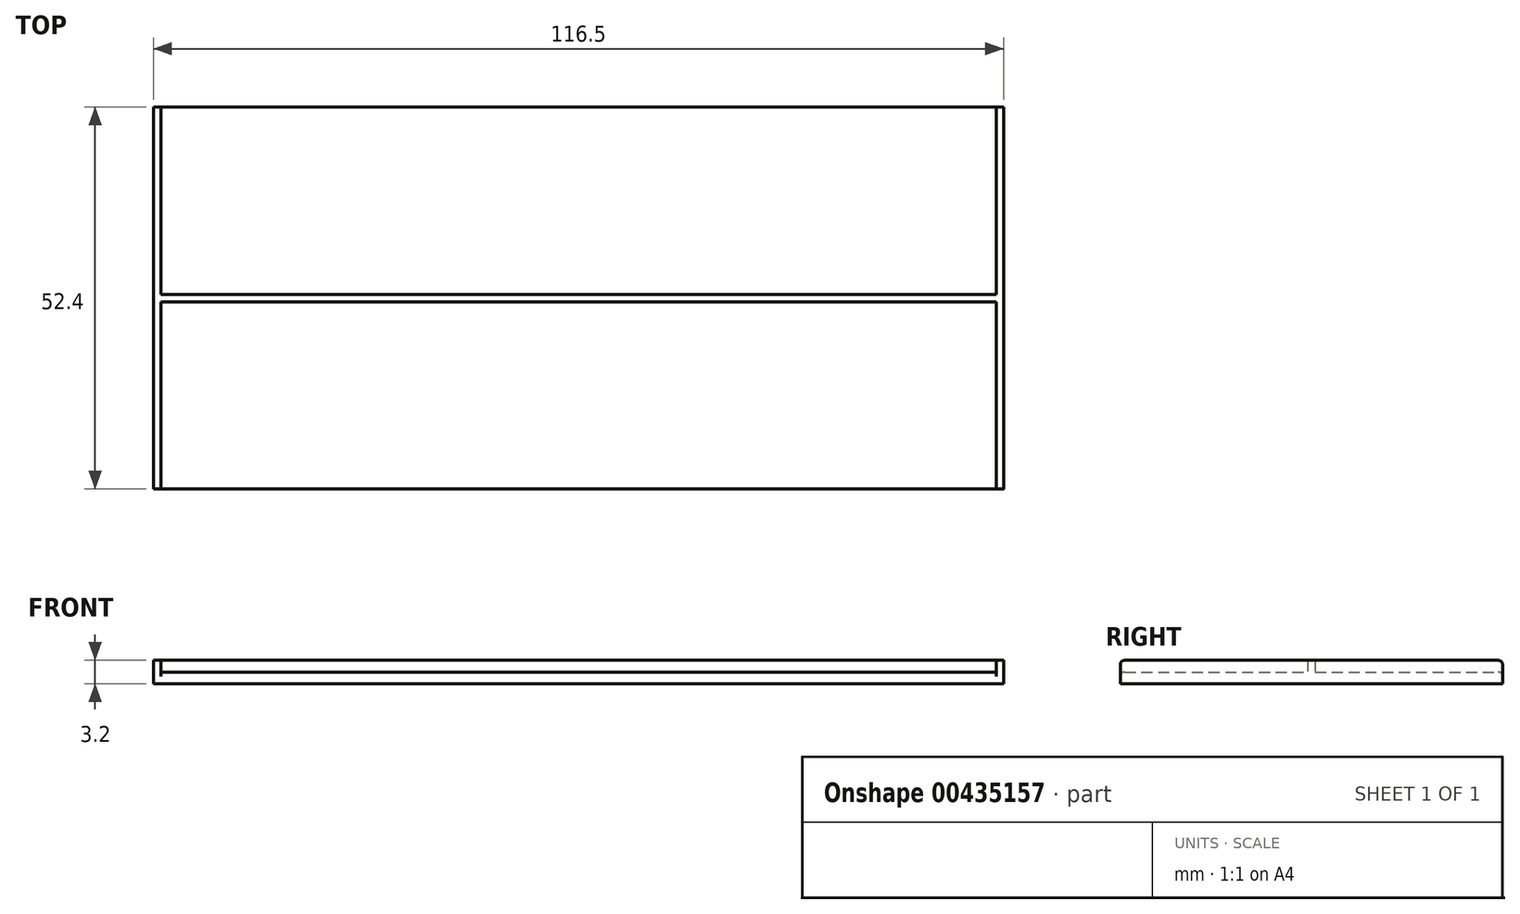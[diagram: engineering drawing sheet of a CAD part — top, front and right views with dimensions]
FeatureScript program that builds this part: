
annotation { "Feature Type Name" : "Feature", "Feature Type Description" : "" }
export const myFeature = defineFeature(function(context is Context, id is Id, definition is map)
    precondition{}
    {
        {
            var Q0;
            Q0=qCreatedBy(makeId("Top.planeOp"),FACE);
            var sketch = newSketch(context, id + "F0", { "sketchPlane" : qUnion([Q0])});
            skLineSegment(sketch, "E0.bottom", {"start": v(0, 0) * mm, "end": v(114.5, 0) * mm});
            skLineSegment(sketch, "E0.top", {"start": v(0, 52.4) * mm, "end": v(114.5, 52.4) * mm});
            skLineSegment(sketch, "E0.left", {"start": v(0, 0) * mm, "end": v(0, 52.4) * mm});
            skLineSegment(sketch, "E0.right", {"start": v(114.5, 0) * mm, "end": v(114.5, 52.4) * mm});
            skSolve(sketch);
        }
        {
            var Q0;
            Q0=makeQuery(id+"F0.imprint","IMPRINT",FACE,{"disambiguationData":[TD([[makeQuery(id+"F0.imprint","IMPRINT",EDGE,{"derivedFrom":sQuery(id+"F0.wireOp",EDGE,"E0.bottom")}),1.0]])]});
            extrude(context, id + "F1", {"entities" : qUnion([Q0]), "depth" : 1.6 * mm});
        }
        {
            var Q0;
            Q0=makeQuery(id+"F1.opExtrude","CAP_EDGE",EDGE,{"disambiguationData":[OSD([sQuery(id+"F0.wireOp",EDGE,"E0.bottom")])],"isStart":false});
            var Q1;
            Q1=makeQuery(id+"F1.opExtrude","CAP_EDGE",EDGE,{"disambiguationData":[OSD([sQuery(id+"F0.wireOp",EDGE,"E0.top")])],"isStart":false});
            fillet(context, id + "F2", {"entities" : qUnion([Q0, Q1]), "radius" : 0.6 * mm, "tangentPropagation" : true, "allowEdgeOverflow" : false});
        }
        {
            var Q0;
            Q0=makeQuery(id+"F1.opExtrude","SWEPT_FACE",FACE,{"disambiguationData":[OSD([sQuery(id+"F0.wireOp",EDGE,"E0.right")])]});
            var sketch = newSketch(context, id + "F3", { "sketchPlane" : qUnion([Q0])});
            skLineSegment(sketch, "E1.bottom", {"start": v(0, 0) * mm, "end": v(52.4, 0) * mm});
            skLineSegment(sketch, "E1.top", {"start": v(0, 3.2) * mm, "end": v(52.4, 3.2) * mm});
            skLineSegment(sketch, "E1.left", {"start": v(0, 0) * mm, "end": v(0, 3.2) * mm});
            skLineSegment(sketch, "E1.right", {"start": v(52.4, 0) * mm, "end": v(52.4, 3.2) * mm});
            skSolve(sketch);
        }
        {
            var Q0;
            Q0 = qSketchRegion(id + "F3", true);
            extrude(context, id + "F4", {"entities" : qUnion([Q0]), "operationType" : NewBodyOperationType.ADD, "depth" : 1 * mm});
        }
        {
            var Q0;
            Q0=makeQuery(id+"F4.opExtrude","SWEPT_EDGE",EDGE,{"disambiguationData":[OSD([sQuery(id+"F3.wireOp",EDGE,"E1.top"),sQuery(id+"F3.wireOp",EDGE,"E1.right")])]});
            var Q1;
            Q1=makeQuery(id+"F4.opExtrude","SWEPT_EDGE",EDGE,{"disambiguationData":[OSD([sQuery(id+"F3.wireOp",EDGE,"E1.top"),sQuery(id+"F3.wireOp",EDGE,"E1.left")])]});
            fillet(context, id + "F5", {"entities" : qUnion([Q0, Q1]), "radius" : 0.6 * mm, "tangentPropagation" : true, "allowEdgeOverflow" : false});
        }
        {
            var Q0;
            Q0=makeQuery(id+"F1.opExtrude","SWEPT_FACE",FACE,{"disambiguationData":[OSD([sQuery(id+"F0.wireOp",EDGE,"E0.left")])]});
            var sketch = newSketch(context, id + "F6", { "sketchPlane" : qUnion([Q0])});
            skLineSegment(sketch, "E2.bottom", {"start": v(-52.4, 0) * mm, "end": v(0, 0) * mm});
            skLineSegment(sketch, "E2.top", {"start": v(-52.4, 3.2) * mm, "end": v(0, 3.2) * mm});
            skLineSegment(sketch, "E2.left", {"start": v(-52.4, 0) * mm, "end": v(-52.4, 3.2) * mm});
            skLineSegment(sketch, "E2.right", {"start": v(0, 0) * mm, "end": v(0, 3.2) * mm});
            skSolve(sketch);
        }
        {
            var Q0;
            Q0 = qSketchRegion(id + "F6", true);
            extrude(context, id + "F7", {"entities" : qUnion([Q0]), "operationType" : NewBodyOperationType.ADD, "depth" : 1 * mm});
        }
        {
            var Q0;
            Q0=makeQuery(id+"F7.opExtrude","SWEPT_EDGE",EDGE,{"disambiguationData":[OSD([sQuery(id+"F6.wireOp",EDGE,"E2.top"),sQuery(id+"F6.wireOp",EDGE,"E2.right")])]});
            var Q1;
            Q1=makeQuery(id+"F7.opExtrude","SWEPT_EDGE",EDGE,{"disambiguationData":[OSD([sQuery(id+"F6.wireOp",EDGE,"E2.top"),sQuery(id+"F6.wireOp",EDGE,"E2.left")])]});
            fillet(context, id + "F8", {"entities" : qUnion([Q0, Q1]), "radius" : 0.6 * mm, "tangentPropagation" : true, "allowEdgeOverflow" : false});
        }
        {
            var Q0;
            Q0=makeQuery(id+"F1.opExtrude","CAP_FACE",FACE,{"disambiguationData":[OSD([sQuery(id+"F0.wireOp",EDGE,"E0.bottom"),sQuery(id+"F0.wireOp",EDGE,"E0.top"),sQuery(id+"F0.wireOp",EDGE,"E0.left"),sQuery(id+"F0.wireOp",EDGE,"E0.right")])],"isStart":false});
            var sketch = newSketch(context, id + "F9", { "sketchPlane" : qUnion([Q0])});
            skLineSegment(sketch, "E3.bottom", {"start": v(0, 25.7) * mm, "end": v(114.5, 25.7) * mm});
            skLineSegment(sketch, "E3.top", {"start": v(0, 26.7) * mm, "end": v(114.5, 26.7) * mm});
            skLineSegment(sketch, "E3.left", {"start": v(0, 25.7) * mm, "end": v(0, 26.7) * mm});
            skLineSegment(sketch, "E3.right", {"start": v(114.5, 22.85) * mm, "end": v(114.5, 26.2) * mm});
            skSolve(sketch);
        }
        {
            var Q0;
            {var subQ1=sQuery(id+"F9.wireOp",EDGE,"E3.bottom");Q0=makeQuery(id+"F9.imprint","IMPRINT",FACE,{"disambiguationData":[TD([[makeQuery(id+"F9.imprint","IMPRINT",EDGE,{"derivedFrom":subQ1}),1.0]])]});}
            var Q1;
            Q1=makeQuery(id+"F4.opExtrude","SWEPT_FACE",FACE,{"disambiguationData":[OSD([sQuery(id+"F3.wireOp",EDGE,"E1.top")])]});
            extrude(context, id + "F10", {"entities" : qUnion([Q0]), "operationType" : NewBodyOperationType.ADD, "endBound" : BoundingType.UP_TO_SURFACE, "endBoundEntityFace" : qUnion([Q1]), "depth" : 25 * mm});
        }
    });
